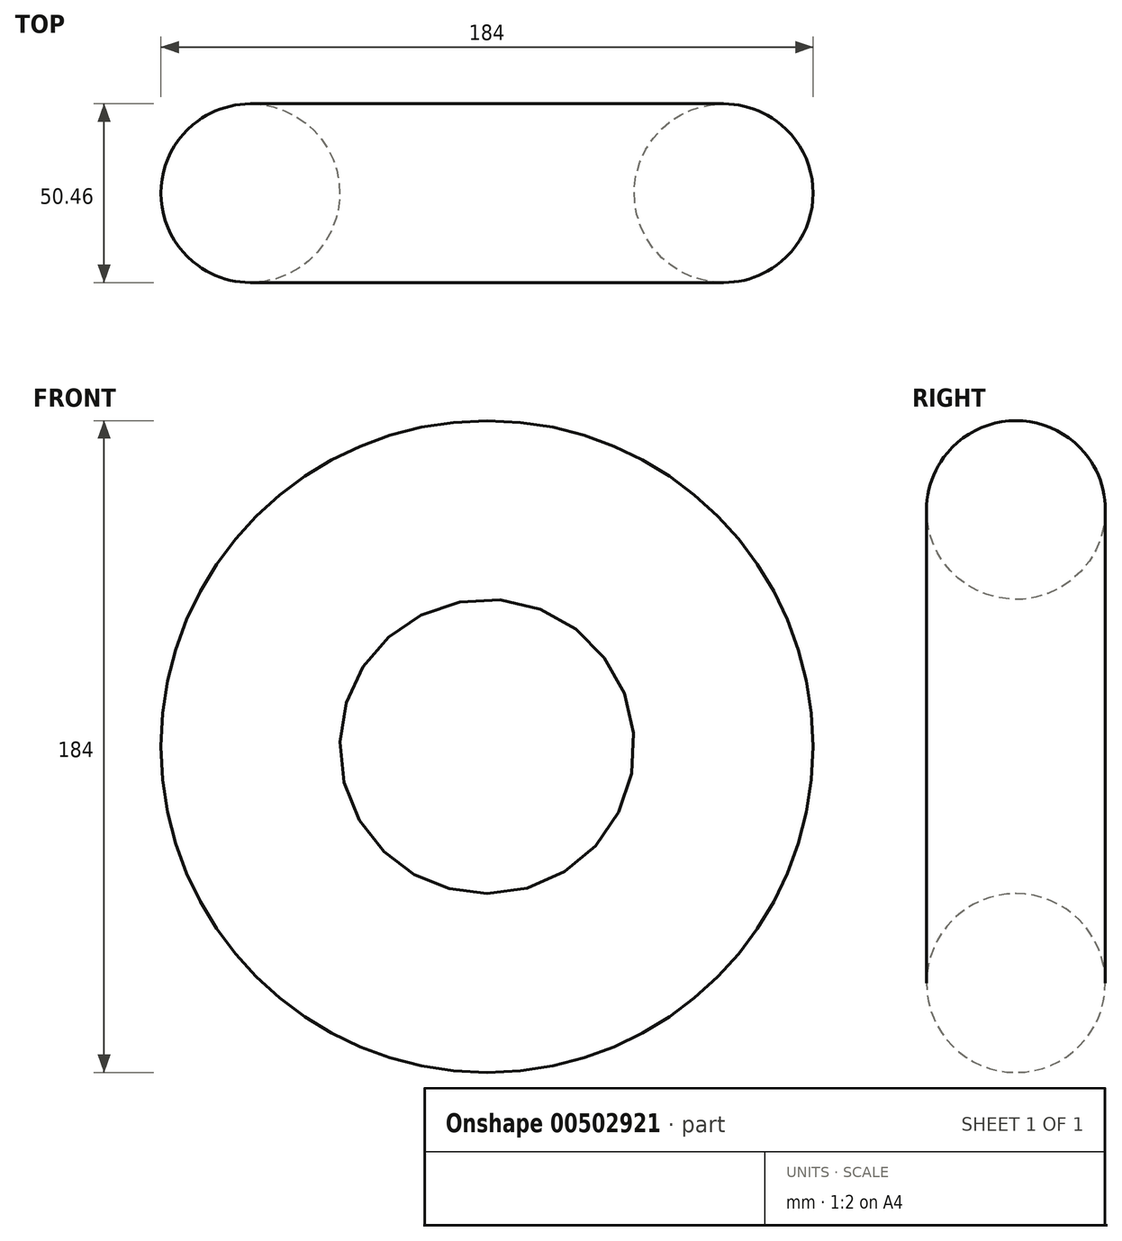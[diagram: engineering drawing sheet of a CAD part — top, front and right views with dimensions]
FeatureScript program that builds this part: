
annotation { "Feature Type Name" : "Feature", "Feature Type Description" : "" }
export const myFeature = defineFeature(function(context is Context, id is Id, definition is map)
    precondition{}
    {
        {
            var Q0;
            Q0=qCreatedBy(makeId("Top.planeOp"),FACE);
            var sketch = newSketch(context, id + "F0", { "sketchPlane" : qUnion([Q0])});
            skCircle(sketch, "E0", {"center": v(-66.77, 0) * mm, "radius": 25.23 * mm});
            skLineSegment(sketch, "E1", {"start": v(0, 0) * mm, "end": v(0, 34.82) * mm, "construction": true});
            skSolve(sketch);
        }
        {
            var Q0;
            Q0 = qSketchRegion(id + "F0", true);
            var Q1;
            Q1=sQuery(id+"F0.wireOp",EDGE,"E1");
            revolve(context, id + "F1", {"entities" : qUnion([Q0]), "axis" : qUnion([Q1]), "revolveType" : RevolveType.FULL});
        }
    });
